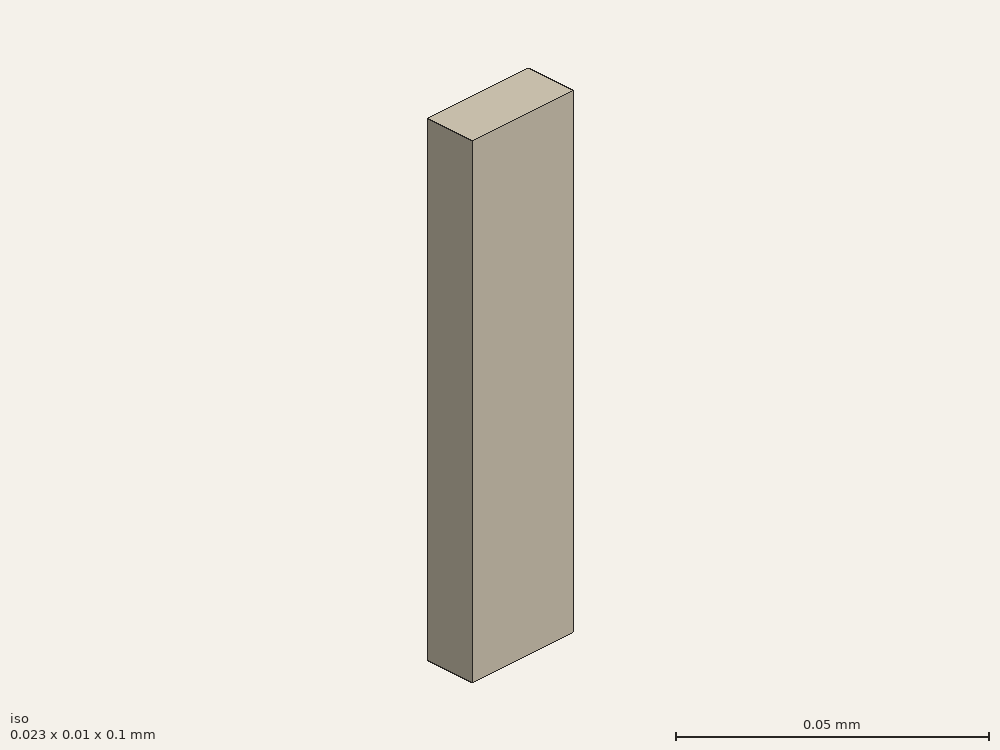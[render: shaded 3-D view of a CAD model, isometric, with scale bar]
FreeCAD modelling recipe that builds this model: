
FCSTD DOCUMENT  (FreeCAD 0.21R33694 (Git))
Label: straight
License: All rights reserved
LicenseURL: http://en.wikipedia.org/wiki/All_rights_reserved
objects: Part::Part2DObjectPython×9, App::FeaturePython×8, Part::Extrusion×1, Part::FeaturePython×1
note: 11 computed .brp shape members not serialized (recipe doc carries the construction recipe); baked Part::Feature solids carry a one-line shape summary decoded from their .brp

FEATURE [Part::Part2DObjectPython] Rectangle  # Draft 2D object (typed FeaturePython)
  Area = 232.258
  ChamferSize = 0
  Columns = 1
  FilletRadius = 0
  Height = 10.16
  Length = 22.86
  MakeFace = true
  Placement = pos=(-11.43,-5.08,0) rot=(0,0,1;0rad)
  Rows = 1
FEATURE [Part::Extrusion] Extrude
  Base = -> Rectangle
  Dir = (0,0,1)
  DirMode = 2
  FaceMakerClass = Part::FaceMakerBullseye
  LengthFwd = 100
  LengthRev = 0
  Solid = false
  Symmetric = false
FEATURE [Part::FeaturePython] Clone  label="scaled"  # Draft clone (typed FeaturePython)
  AttacherType = Attacher::AttachEngine3D
  Fuse = false
  Objects = -> [Extrude]
  Scale = (0.001,0.001,0.001)
FEATURE [Part::Part2DObjectPython] Rectangle001  label="_Pport1"  # Draft 2D object (typed FeaturePython)
  Area = 0.000232258
  ChamferSize = 0
  Columns = 1
  FilletRadius = 0
  Height = 0.01016
  Length = 0.02286
  MakeFace = true
  Placement = pos=(-0.01143,-0.00508,0.1) rot=(0,0,1;0rad)
  Rows = 1
FEATURE [Part::Part2DObjectPython] Line  label="_Pv1"  # Draft 2D object (typed FeaturePython)
  Area = 0
  ChamferSize = 0
  Closed = false
  End = (-1.8e-15,0.00508,0.1)
  FilletRadius = 0
  Length = 0.01016
  MakeFace = true
  Placement = pos=(0,-0.00508,0.1) rot=(0,0,1;0rad)
  Points = (2) [(0,0,0),(-1.77605e-15,0.01016,0)]
  Start = (0,-0.00508,0.1)
  Subdivisions = 0
FEATURE [Part::Part2DObjectPython] Rectangle002  label="_Pport2"  # Draft 2D object (typed FeaturePython)
  Area = 0.000232258
  ChamferSize = 0
  Columns = 1
  FilletRadius = 0
  Height = 0.01016
  Length = 0.02286
  MakeFace = true
  Placement = pos=(-0.01143,-0.00508,0) rot=(0,0,1;0rad)
  Rows = 1
FEATURE [Part::Part2DObjectPython] Line001  label="_Pv2"  # Draft 2D object (typed FeaturePython)
  Area = 0
  ChamferSize = 0
  Closed = false
  End = (0,0.00508,0)
  FilletRadius = 0
  Length = 0.01016
  MakeFace = true
  Placement = pos=(0,-0.00508,0) rot=(0,0,1;0rad)
  Points = (2) [(0,0,0),(3.1106e-19,0.01016,0)]
  Start = (0,-0.00508,0)
  Subdivisions = 0
FEATURE [App::FeaturePython] Text  label="_Sinput(PV){port1}"  # WARN: FeaturePython — macro-defined, semantics opaque (R4)
  Placement = pos=(0.0413747,-0.017509,0) rot=(0,0,1;0rad)
  Text = .
FEATURE [App::FeaturePython] Text001  label="_Soutput(PV){port2}"  # WARN: FeaturePython — macro-defined, semantics opaque (R4)
  Placement = pos=(0.0413747,-0.017509,0) rot=(0,0,1;0rad)
  Text = .
FEATURE [App::FeaturePython] Text002  label="_Linput(1,voltage){v1}"  # WARN: FeaturePython — macro-defined, semantics opaque (R4)
  Placement = pos=(0.0413747,-0.017509,0) rot=(0,0,1;0rad)
  Text = .
FEATURE [App::FeaturePython] Text003  label="_Loutput(2,voltage){v2}"  # WARN: FeaturePython — macro-defined, semantics opaque (R4)
  Placement = pos=(0.0413747,-0.017509,0) rot=(0,0,1;0rad)
  Text = .
FEATURE [Part::Part2DObjectPython] Rectangle003  label="_Pside1"  # Draft 2D object (typed FeaturePython)
  Area = 0.002286
  ChamferSize = 0
  Columns = 1
  FilletRadius = 0
  Height = 0.1
  Length = 0.02286
  MakeFace = true
  Placement = pos=(-0.01143,-0.00508,0) rot=(1,0,0;1.5708rad)
  Rows = 1
FEATURE [Part::Part2DObjectPython] Rectangle004  label="_Pside3"  # Draft 2D object (typed FeaturePython)
  Area = 0.002286
  ChamferSize = 0
  Columns = 1
  FilletRadius = 0
  Height = 0.1
  Length = 0.02286
  MakeFace = true
  Placement = pos=(-0.01143,0.00508,0) rot=(1,0,0;1.5708rad)
  Rows = 1
FEATURE [Part::Part2DObjectPython] Rectangle005  label="_Pside2"  # Draft 2D object (typed FeaturePython)
  Area = 0.001016
  ChamferSize = 0
  Columns = 1
  FilletRadius = 0
  Height = 0.1
  Length = 0.01016
  MakeFace = true
  Placement = pos=(0.01143,-0.00508,0) rot=(0.57735,0.57735,0.57735;2.0944rad)
  Rows = 1
FEATURE [Part::Part2DObjectPython] Rectangle006  label="_Pside4"  # Draft 2D object (typed FeaturePython)
  Area = 0.001016
  ChamferSize = 0
  Columns = 1
  FilletRadius = 0
  Height = 0.1
  Length = 0.01016
  MakeFace = true
  Placement = pos=(-0.01143,-0.00508,0) rot=(0.57735,0.57735,0.57735;2.0944rad)
  Rows = 1
FEATURE [App::FeaturePython] Text004  label="_BCu1(SI,copper){side1}"  # WARN: FeaturePython — macro-defined, semantics opaque (R4)
  Placement = pos=(0.0413747,-0.017509,0) rot=(0,0,1;0rad)
  Text = .
FEATURE [App::FeaturePython] Text005  label="_BCu2(SI,copper){side2}"  # WARN: FeaturePython — macro-defined, semantics opaque (R4)
  Placement = pos=(0.0413747,-0.017509,0) rot=(0,0,1;0rad)
  Text = .
FEATURE [App::FeaturePython] Text006  label="_BCu3(SI,copper){side3}"  # WARN: FeaturePython — macro-defined, semantics opaque (R4)
  Placement = pos=(0.0413747,-0.017509,0) rot=(0,0,1;0rad)
  Text = .
FEATURE [App::FeaturePython] Text007  label="_BCu4(SI,copper){side4}"  # WARN: FeaturePython — macro-defined, semantics opaque (R4)
  Placement = pos=(0.0413747,-0.017509,0) rot=(0,0,1;0rad)
  Text = .
